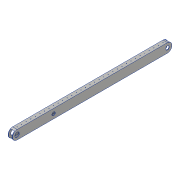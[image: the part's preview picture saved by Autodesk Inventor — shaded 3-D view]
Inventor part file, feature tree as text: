
AUTODESK INVENTOR PART (.ipt)
format: ipt  version: 2018 (Build 220112000, 112)  size: 242,176 bytes
history: native  units: in
note: dims shown in document units (in); Inventor stores cm internally (conversion verified against a paired STEP export)
features: sketch x7, extrude x5, hole x2, projected_geometry x2, shell x1, fillet x1
ambient origin geometry x8: Origin, YZ Plane, XZ Plane, XY Plane, X Axis, Y Axis, Z Axis, Center Point
bodies: Solid1 (feature_tree)
feature tree (18):
  extrude  "Extrusion1"  Depth=2.0in
  shell  "Shell1"  Thickness=35.0in
  hole  "Hole1"  [1 undecoded]
  extrude  "Extrusion2"  Depth=1.0in
  extrude  "Extrusion3"  Depth=1.0in
  extrude  "Extrusion4"  Depth=0.75in
  fillet  "Fillet1"  Radius=1.0in
  extrude  "Extrusion5"  Depth=0.433in
  hole  "Hole5"  [1 undecoded]
  sketch  "Sketch1"  dims[d0=1.0in d1=2.0in d2=35.0in d3=0.0in]
  sketch  "Sketch2"  dims[d4=0.1in d5=0.5in]
  sketch  "Sketch6"  dims[d6=0.5in d7=14.5669in d9=1.0in d10=0.3937in d12=1.0in]
  sketch  "Sketch7"  dims[d14=0.1in d15=0.75in d16=0.375in d17=0.25in d18=0.5635in d19=2.0in d20=0.8108in d48=1.0in]
  projected_geometry  "Projected Loop2"
  sketch  "Sketch8"  dims[d49=1.0in d50=0.75in d51=1.0in d52=0.0in]
  sketch  "Sketch9"  dims[d53=0.433in d54=0.433in]
  projected_geometry  "Projected Loop3"
  sketch  "Sketch10"  dims[d55=1.0in d56=0.0in d57=1.0in d58=0.75in d59=1.0in d60=1.0in d61=0.0in d62=1.0in d63=1.0in d64=1.0in d65=0.0in d66=8.0in d67=0.75in d68=0.75in d69=0.375in d70=0.25in d71=0.5635in d72=1.0in d73=0.8108in]
note: 2 required parameter values undecoded (feature->parameter linkage not recoverable at this tier; creation-order binding heuristic only, values carry confidence <= 0.55)
